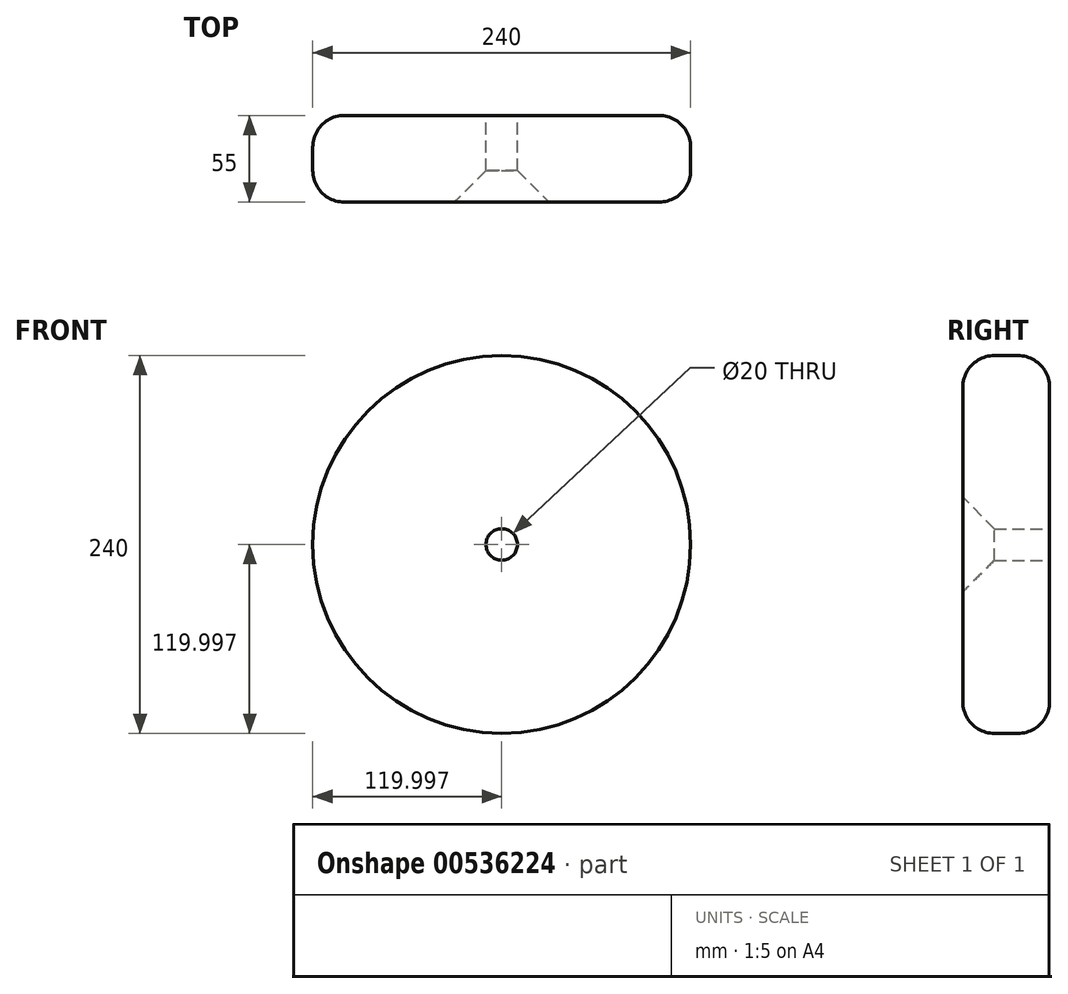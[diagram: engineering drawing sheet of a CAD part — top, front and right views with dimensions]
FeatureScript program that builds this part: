
annotation { "Feature Type Name" : "Feature", "Feature Type Description" : "" }
export const myFeature = defineFeature(function(context is Context, id is Id, definition is map)
    precondition{}
    {
        {
            var Q0;
            Q0=qCreatedBy(makeId("Front.planeOp"),FACE);
            var sketch = newSketch(context, id + "F0", { "sketchPlane" : qUnion([Q0])});
            skCircle(sketch, "E0", {"center": v(-49.97, 9.97) * mm, "radius": 120 * mm});
            skCircle(sketch, "E1", {"center": v(-49.97, 9.97) * mm, "radius": 10 * mm});
            skSolve(sketch);
        }
        {
            var Q0;
            Q0=makeQuery(id+"F0.imprint","IMPRINT",FACE,{"disambiguationData":[TD([[makeQuery(id+"F0.imprint","IMPRINT",EDGE,{"derivedFrom":sQuery(id+"F0.wireOp",EDGE,"E0")}),1.0]])]});
            extrude(context, id + "F1", {"entities" : qUnion([Q0]), "depth" : 55 * mm, "offsetDistance" : 25 * mm});
        }
        {
            var Q0;
            Q0=makeQuery(id+"F1.opExtrude","CAP_EDGE",EDGE,{"disambiguationData":[OSD([sQuery(id+"F0.wireOp",EDGE,"E0")])],"isStart":false});
            var Q1;
            Q1=makeQuery(id+"F1.opExtrude","CAP_EDGE",EDGE,{"disambiguationData":[OSD([sQuery(id+"F0.wireOp",EDGE,"E0")])],"isStart":true});
            fillet(context, id + "F2", {"entities" : qUnion([Q0, Q1]), "radius" : 20 * mm, "tangentPropagation" : true, "allowEdgeOverflow" : false});
        }
        {
            var Q0;
            Q0=makeQuery(id+"F1.opExtrude","CAP_EDGE",EDGE,{"disambiguationData":[OSD([sQuery(id+"F0.wireOp",EDGE,"E1")])],"isStart":false});
            chamfer(context, id + "F3", {"entities" : qUnion([Q0]), "width" : 20 * mm, "tangentPropagation" : true});
        }
        {
            var Q0;
            {var subQ0=sQuery(id+"F0.wireOp",EDGE,"E1");Q0=makeQuery(id+"F3.opChamfer","BLEND_EDGE",EDGE,{"blendedFrom":[makeQuery(id+"F1.opExtrude","CAP_EDGE",EDGE,{"disambiguationData":[OSD([subQ0])],"isStart":false}),makeQuery(id+"F1.opExtrude","CAP_FACE",FACE,{"disambiguationData":[OSD([sQuery(id+"F0.wireOp",EDGE,"E0"),subQ0])],"isStart":false})],"blendedInto":[makeQuery(id+"F1.opExtrude","CAP_FACE",FACE,{"disambiguationData":[OSD([sQuery(id+"F0.wireOp",EDGE,"E0"),subQ0])],"isStart":false})]});}
            var Q1;
            {var subQ0=sQuery(id+"F0.wireOp",EDGE,"E0");Q1=makeQuery(id+"F2.opFillet","BLEND_EDGE",EDGE,{"blendedFrom":[makeQuery(id+"F1.opExtrude","CAP_EDGE",EDGE,{"disambiguationData":[OSD([subQ0])],"isStart":false}),makeQuery(id+"F1.opExtrude","CAP_FACE",FACE,{"disambiguationData":[OSD([subQ0,sQuery(id+"F0.wireOp",EDGE,"E1")])],"isStart":false})],"blendedInto":[makeQuery(id+"F1.opExtrude","CAP_FACE",FACE,{"disambiguationData":[OSD([subQ0,sQuery(id+"F0.wireOp",EDGE,"E1")])],"isStart":false})]});}
            fillet(context, id + "F4", {"entities" : qUnion([Q0, Q1]), "radius" : 5 * mm, "tangentPropagation" : true, "allowEdgeOverflow" : false});
        }
    });
